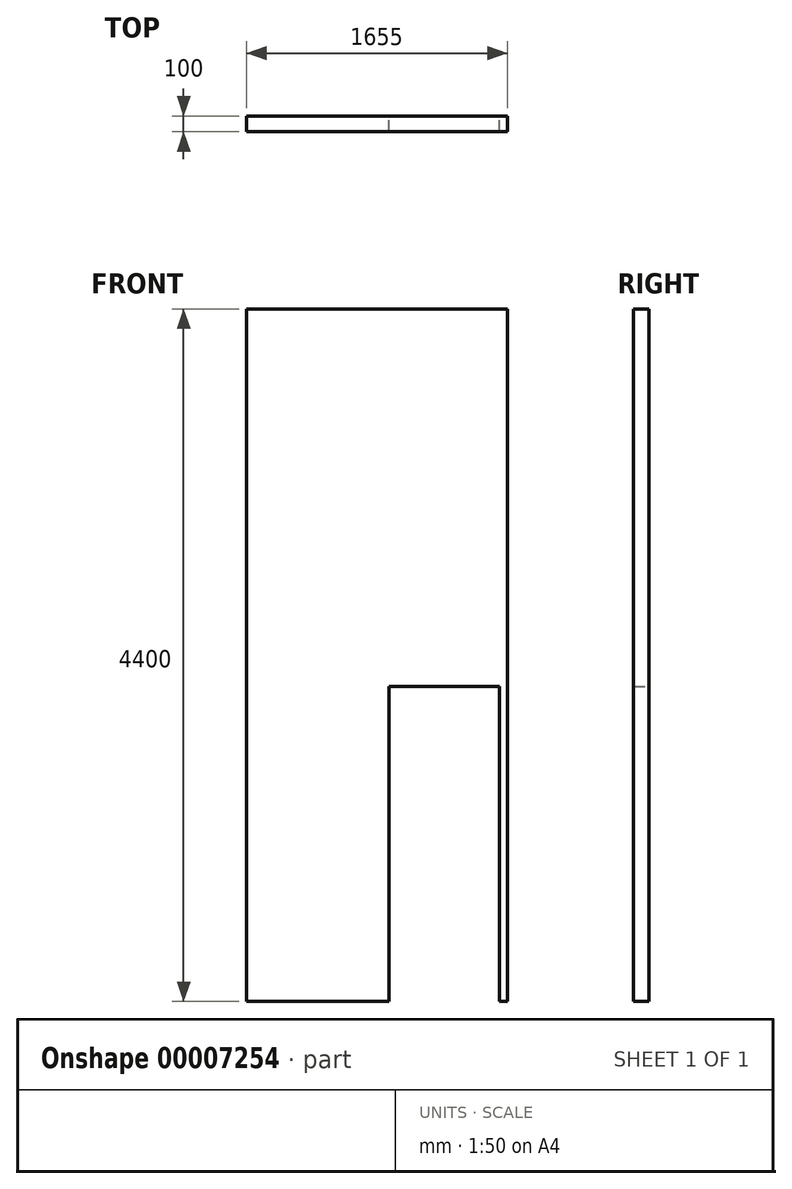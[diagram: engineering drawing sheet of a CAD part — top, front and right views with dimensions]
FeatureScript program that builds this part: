
annotation { "Feature Type Name" : "Feature", "Feature Type Description" : "" }
export const myFeature = defineFeature(function(context is Context, id is Id, definition is map)
    precondition{}
    {
        {
            var Q0;
            Q0=qCreatedBy(makeId("Front.planeOp"),FACE);
            var sketch = newSketch(context, id + "F0", { "sketchPlane" : qUnion([Q0])});
            skLineSegment(sketch, "E0", {"start": v(0, 0) * mm, "end": v(0, 4400) * mm});
            skLineSegment(sketch, "E1", {"start": v(0, 4400) * mm, "end": v(1655, 4400) * mm});
            skLineSegment(sketch, "E2", {"start": v(1655, 4400) * mm, "end": v(1655, 0) * mm});
            skLineSegment(sketch, "E3", {"start": v(1655, 0) * mm, "end": v(1605, 0) * mm});
            skLineSegment(sketch, "E4", {"start": v(1605, 0) * mm, "end": v(1605, 2000) * mm});
            skLineSegment(sketch, "E5", {"start": v(1605, 2000) * mm, "end": v(905, 2000) * mm});
            skLineSegment(sketch, "E6", {"start": v(905, 2000) * mm, "end": v(905, 0) * mm});
            skLineSegment(sketch, "E7", {"start": v(905, 0) * mm, "end": v(0, 0) * mm});
            skSolve(sketch);
        }
        {
            var Q0;
            Q0=makeQuery(id+"F0.imprint","IMPRINT",FACE,{"disambiguationData":[TD([[makeQuery(id+"F0.imprint","IMPRINT",EDGE,{"derivedFrom":sQuery(id+"F0.wireOp",EDGE,"E0")}),-1.0]])]});
            extrude(context, id + "F1", {"entities" : qUnion([Q0]), "depth" : 100 * mm});
        }
    });
